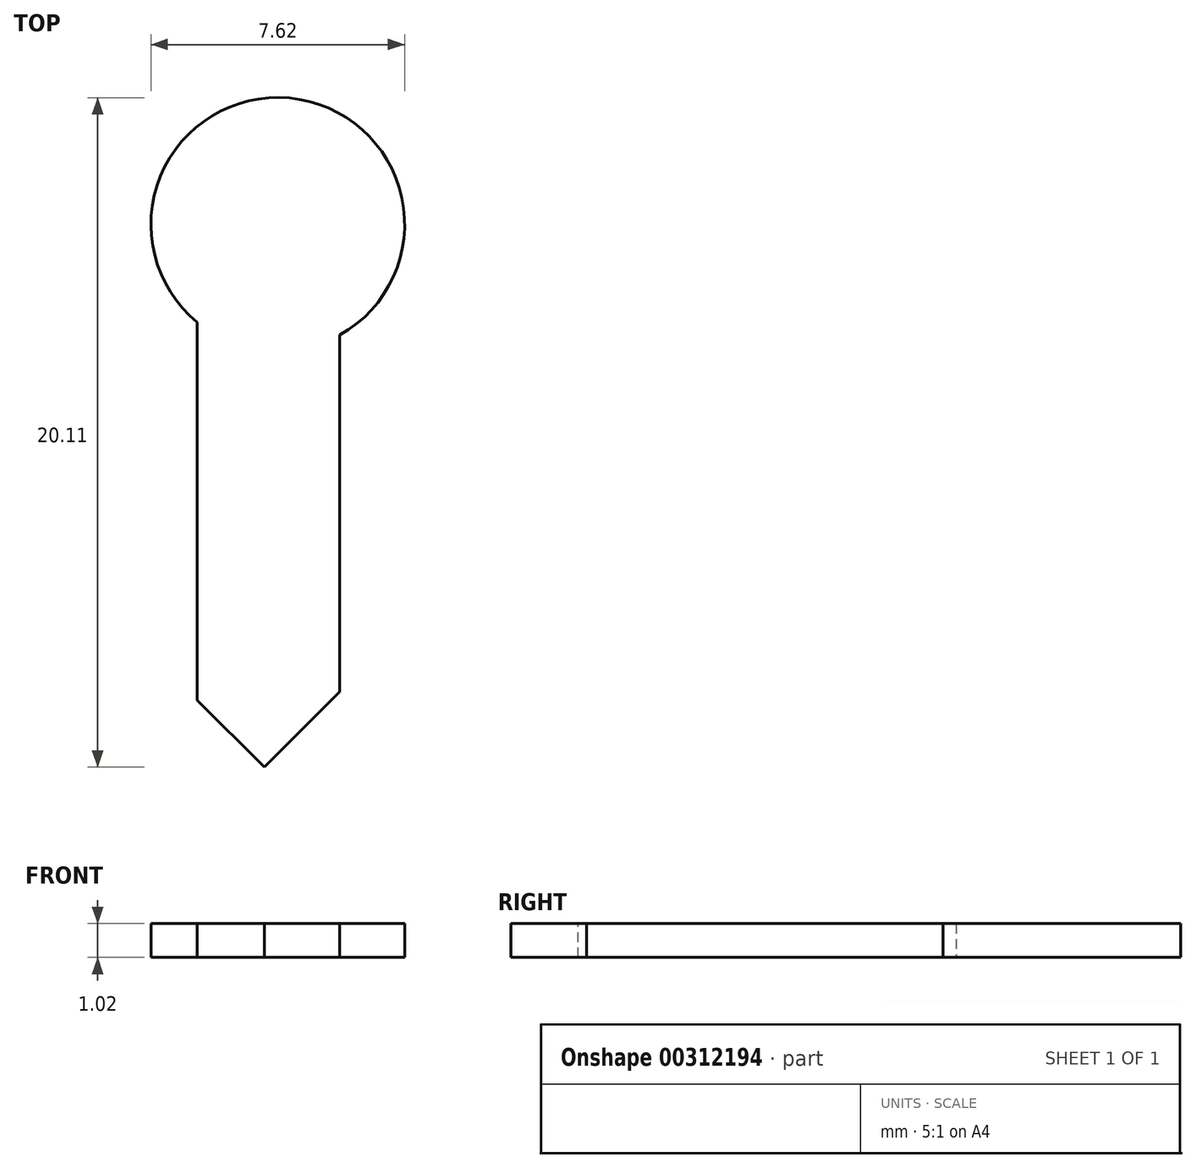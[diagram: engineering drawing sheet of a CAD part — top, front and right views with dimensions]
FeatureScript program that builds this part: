
annotation { "Feature Type Name" : "Feature", "Feature Type Description" : "" }
export const myFeature = defineFeature(function(context is Context, id is Id, definition is map)
    precondition{}
    {
        {
            var Q0;
            Q0=qCreatedBy(makeId("Top.planeOp"),FACE);
            var sketch = newSketch(context, id + "F0", { "sketchPlane" : qUnion([Q0])});
            skCircle(sketch, "E0", {"center": v(-29.28, 26) * mm, "radius": 3.81 * mm});
            skSolve(sketch);
        }
        {
            var Q0;
            Q0 = qSketchRegion(id + "F0", true);
            extrude(context, id + "F1", {"entities" : qUnion([Q0]), "depth" : 1.02 * mm});
        }
        {
            var Q0;
            Q0=qCreatedBy(makeId("Top.planeOp"),FACE);
            var sketch = newSketch(context, id + "F2", { "sketchPlane" : qUnion([Q0])});
            skLineSegment(sketch, "E1.bottom", {"start": v(-31.7, 23.1) * mm, "end": v(-27.42, 23.1) * mm});
            skLineSegment(sketch, "E1.top", {"start": v(-31.7, 9.68) * mm, "end": v(-27.42, 9.68) * mm});
            skLineSegment(sketch, "E1.left", {"start": v(-31.7, 23.1) * mm, "end": v(-31.7, 9.68) * mm});
            skLineSegment(sketch, "E1.right", {"start": v(-27.42, 23.1) * mm, "end": v(-27.42, 9.68) * mm});
            skSolve(sketch);
        }
        {
            var Q0;
            Q0=makeQuery(id+"F2.imprint","IMPRINT",FACE,{"disambiguationData":[TD([[makeQuery(id+"F2.imprint","IMPRINT",EDGE,{"derivedFrom":sQuery(id+"F2.wireOp",EDGE,"E1.bottom")}),-1.0]])]});
            extrude(context, id + "F3", {"entities" : qUnion([Q0]), "operationType" : NewBodyOperationType.ADD, "depth" : 1.02 * mm});
        }
        {
            var Q0;
            Q0=makeQuery(id+"F3.opExtrude","SWEPT_EDGE",EDGE,{"disambiguationData":[OSD([sQuery(id+"F2.wireOp",EDGE,"E1.top"),sQuery(id+"F2.wireOp",EDGE,"E1.right")])]});
            chamfer(context, id + "F4", {"entities" : qUnion([Q0]), "width" : 2.3 * mm, "tangentPropagation" : true});
        }
        {
            var Q0;
            Q0=makeQuery(id+"F3.opExtrude","SWEPT_EDGE",EDGE,{"disambiguationData":[OSD([sQuery(id+"F2.wireOp",EDGE,"E1.top"),sQuery(id+"F2.wireOp",EDGE,"E1.left")])]});
            chamfer(context, id + "F5", {"entities" : qUnion([Q0]), "width" : 2.03 * mm, "tangentPropagation" : true});
        }
    });
